# Revit family: Holyoake - Series TLC
name_source: partatom
category: Air Terminals
revit_build: Autodesk Revit 2014 (Build: 20140709_2115(x64)
units: mm (PartAtom-declared; Revit-internal decimal feet)

## types (1)
- Type 1
    Arc Angle Half = 14.32°
    Arc Length = 200 mm  [stored 0.656168 ft]
    Back Blade Face = 362 mm
    Blade Radius = 400 mm  [stored 1.31234 ft]
    Blade Width = 400 mm  [stored 1.31234 ft]
    Description = https://productspec.net
    Desired Height = 4000 mm  [stored 13.1234 ft]
    Desired Radius = 400 mm  [stored 1.31234 ft]
    Desired Width = 400 mm  [stored 1.31234 ft]
    Height = 185 mm
    Manufacturer = Holyoake
    Maximum Height = 200 mm  [stored 0.656168 ft]
    Maximum Radius = 1000 mm  [stored 3.28084 ft]
    Maximum Width = 600 mm  [stored 1.9685 ft]
    Minimum Height = 150 mm  [stored 0.492126 ft]
    Minimum Radius = 300 mm  [stored 0.984252 ft]
    Minimum Width = 125 mm
    Nominal W = 400 mm  [stored 1.31234 ft]
    Radius = 400 mm  [stored 1.31234 ft]
    Round Value Height = 4
    Round Value Radius = 8
    Type Comments = TLC Series

note: [stored X ft] marks values corroborated as IEEE doubles in the binary element streams (Revit-internal decimal feet)

## geometry (parser evidence)
native form markers: Sweep x17
no freeform markers — native parametric forms only
